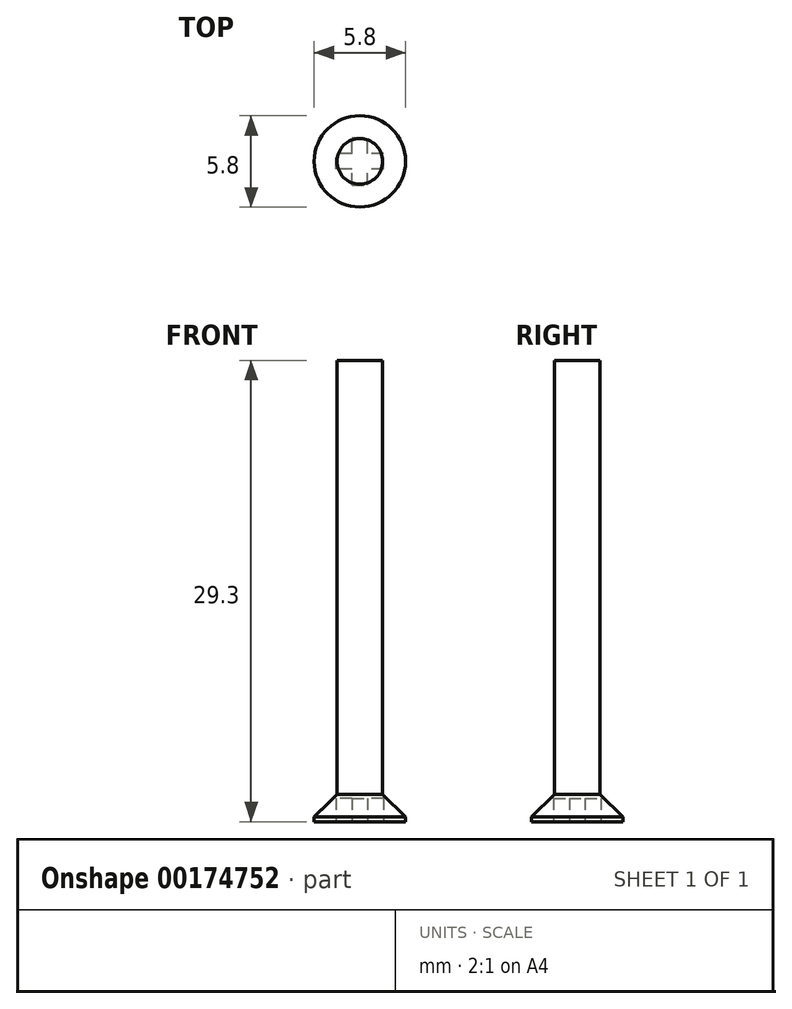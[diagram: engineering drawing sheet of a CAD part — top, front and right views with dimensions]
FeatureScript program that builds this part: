
annotation { "Feature Type Name" : "Feature", "Feature Type Description" : "" }
export const myFeature = defineFeature(function(context is Context, id is Id, definition is map)
    precondition{}
    {
        {
            var Q0;
            Q0=qCreatedBy(makeId("Top.planeOp"),FACE);
            var sketch = newSketch(context, id + "F0", { "sketchPlane" : qUnion([Q0])});
            skCircle(sketch, "E0", {"center": v(0, 0) * mm, "radius": 1.45 * mm});
            skSolve(sketch);
        }
        {
            var Q0;
            Q0=qSketchRegion(id+"F0",true);
            extrude(context, id + "F1", {"entities" : qUnion([Q0]), "offsetDistance" : 25 * mm, "depth" : 27.5 * mm});
        }
        {
            var Q0;
            Q0=qCreatedBy(makeId("Top.planeOp"),FACE);
            var sketch = newSketch(context, id + "F2", { "sketchPlane" : qUnion([Q0])});
            skCircle(sketch, "E1", {"center": v(0, 0) * mm, "radius": 2.9 * mm});
            skSolve(sketch);
        }
        {
            var Q0;
            Q0=qSketchRegion(id+"F2",true);
            extrude(context, id + "F3", {"entities" : qUnion([Q0]), "operationType" : NewBodyOperationType.ADD, "oppositeDirection" : true, "offsetDistance" : 25 * mm, "depth" : 1.8 * mm});
        }
        {
            var Q0;
            Q0=makeQuery(id+"F3.opExtrude","CAP_FACE",FACE,{"disambiguationData":[OSD([sQuery(id+"F2.wireOp",EDGE,"E1")])],"isStart":false});
            var sketch = newSketch(context, id + "F4", { "sketchPlane" : qUnion([Q0])});
            skLineSegment(sketch, "E2.bottom", {"start": v(1.5, 0.5) * mm, "end": v(-1.5, 0.5) * mm});
            skLineSegment(sketch, "E2.top", {"start": v(1.5, -0.5) * mm, "end": v(-1.5, -0.5) * mm});
            skLineSegment(sketch, "E2.left", {"start": v(1.5, 0.5) * mm, "end": v(1.5, -0.5) * mm});
            skLineSegment(sketch, "E2.right", {"start": v(-1.5, 0.5) * mm, "end": v(-1.5, -0.5) * mm});
            skPoint(sketch, "E2.middle", {"position": v(0, 0) * mm});
            skLineSegment(sketch, "E3.bottom", {"start": v(-0.5, 1.5) * mm, "end": v(0.5, 1.5) * mm});
            skLineSegment(sketch, "E3.top", {"start": v(-0.5, -1.5) * mm, "end": v(0.5, -1.5) * mm});
            skLineSegment(sketch, "E3.left", {"start": v(-0.5, 1.5) * mm, "end": v(-0.5, -1.5) * mm});
            skLineSegment(sketch, "E3.right", {"start": v(0.5, 1.5) * mm, "end": v(0.5, -1.5) * mm});
            skSolve(sketch);
        }
        {
            var Q0;
            Q0=qSketchRegion(id+"F4",true);
            extrude(context, id + "F5", {"entities" : qUnion([Q0]), "operationType" : NewBodyOperationType.REMOVE, "oppositeDirection" : true, "depth" : 1.5 * mm});
        }
        {
            var Q0;
            Q0=makeQuery(id+"F3.opExtrude","CAP_EDGE",EDGE,{"disambiguationData":[OSD([sQuery(id+"F2.wireOp",EDGE,"E1")])],"isStart":true});
            chamfer(context, id + "F6", {"entities" : qUnion([Q0]), "width" : 1.5 * mm, "tangentPropagation" : true});
        }
    });
